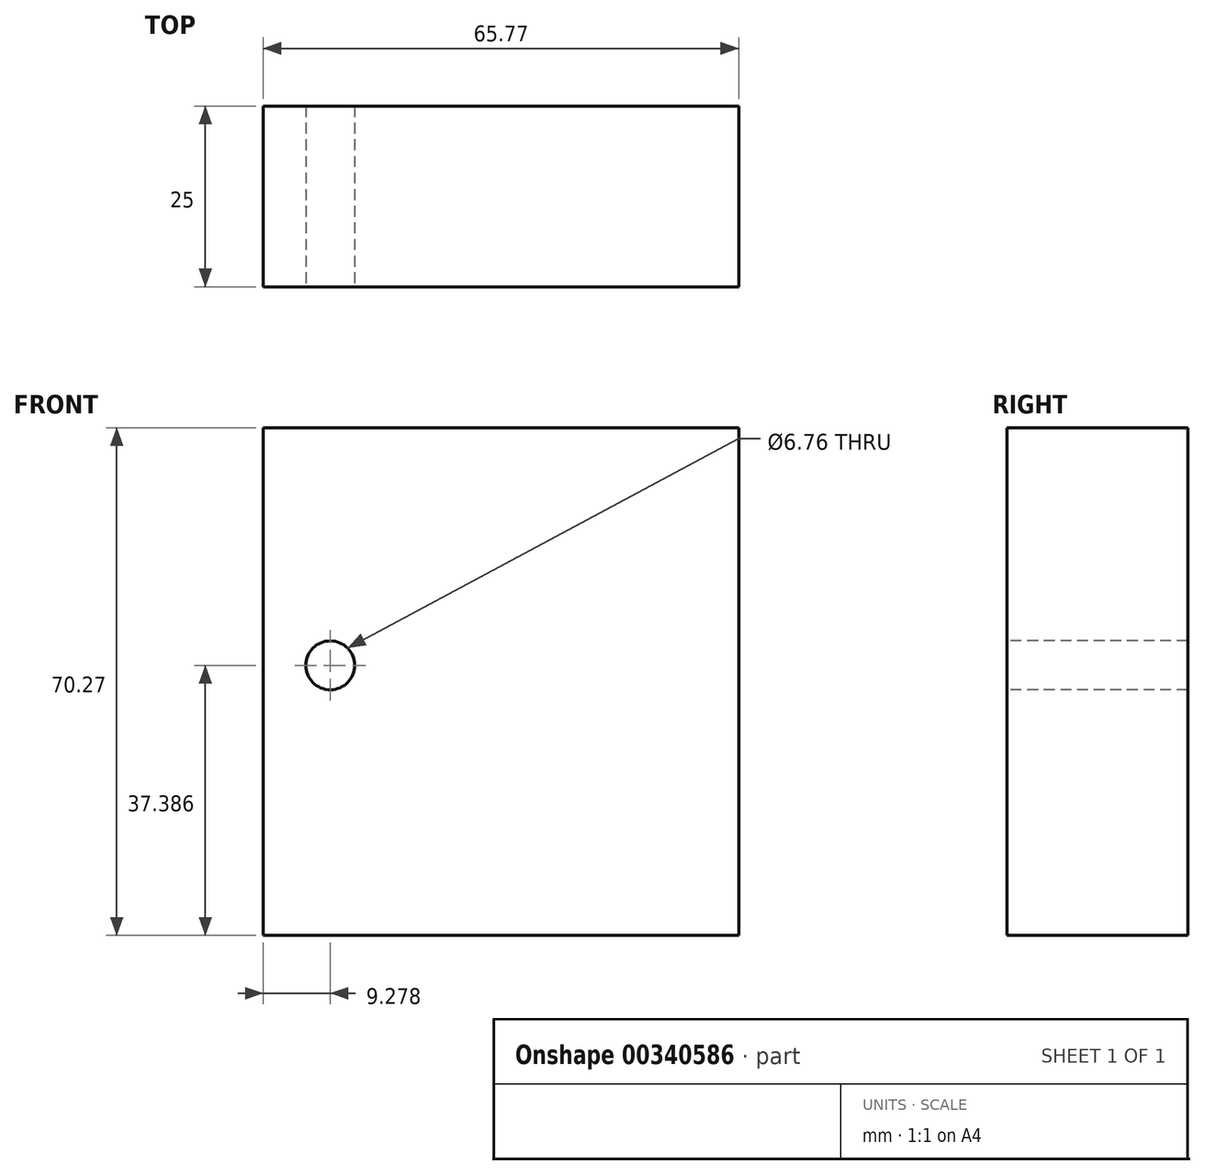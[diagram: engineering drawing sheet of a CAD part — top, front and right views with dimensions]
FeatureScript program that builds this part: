
annotation { "Feature Type Name" : "Feature", "Feature Type Description" : "" }
export const myFeature = defineFeature(function(context is Context, id is Id, definition is map)
    precondition{}
    {
        {
            var Q0;
            Q0=qCreatedBy(makeId("Front.planeOp"),FACE);
            var sketch = newSketch(context, id + "F0", { "sketchPlane" : qUnion([Q0])});
            skLineSegment(sketch, "E0.bottom", {"start": v(-98.66, -12.37) * mm, "end": v(-32.89, -12.37) * mm});
            skLineSegment(sketch, "E0.top", {"start": v(-98.66, 57.9) * mm, "end": v(-32.89, 57.9) * mm});
            skLineSegment(sketch, "E0.left", {"start": v(-98.66, -12.37) * mm, "end": v(-98.66, 57.9) * mm});
            skLineSegment(sketch, "E0.right", {"start": v(-32.89, -12.37) * mm, "end": v(-32.89, 57.9) * mm});
            skPoint(sketch, "E0.middle", {"position": v(-65.77, 22.77) * mm});
            skSolve(sketch);
        }
        {
            var Q0;
            Q0=makeQuery(id+"F0.imprint","IMPRINT",FACE,{"disambiguationData":[TD([[makeQuery(id+"F0.imprint","IMPRINT",EDGE,{"derivedFrom":sQuery(id+"F0.wireOp",EDGE,"E0.bottom")}),1.0]])]});
            extrude(context, id + "F1", {"entities" : qUnion([Q0]), "depth" : 25 * mm});
        }
        {
            var Q0;
            Q0=makeQuery(id+"F1.opExtrude","CAP_FACE",FACE,{"disambiguationData":[OSD([sQuery(id+"F0.wireOp",EDGE,"E0.bottom"),sQuery(id+"F0.wireOp",EDGE,"E0.top"),sQuery(id+"F0.wireOp",EDGE,"E0.left"),sQuery(id+"F0.wireOp",EDGE,"E0.right")])],"isStart":false});
            var sketch = newSketch(context, id + "F2", { "sketchPlane" : qUnion([Q0])});
            skPoint(sketch, "E1", {"position": v(-89.38, 25.02) * mm});
            skSolve(sketch);
        }
        {
            var Q0;
            Q0=sQuery(id+"F2.wireOp",VERTEX,"E1");
            var Q1;
            Q1=makeQuery(id+"F1.opExtrude","SWEPT_BODY",BODY,{"disambiguationData":[OSD([sQuery(id+"F0.wireOp",EDGE,"E0.bottom"),sQuery(id+"F0.wireOp",EDGE,"E0.top"),sQuery(id+"F0.wireOp",EDGE,"E0.left"),sQuery(id+"F0.wireOp",EDGE,"E0.right")])]});
            hole(context, id + "F3", {"style" : HoleStyle.SIMPLE, "endStyle" : HoleEndStyle.THROUGH, "standardTappedOrClearance" : lookupTablePath({ "standard" : "ANSI", "fit" : "Normal (ASME)", "size" : "1/4", "type" : "Clearance" }), "standardBlindInLast" : lookupTablePath({ "fit" : "Free", "standard" : "ANSI", "size" : "1/4", "type" : "Clearance" }), "holeDiameter" : 6.76 * mm, "tappedDepth" : 12 * mm, "tapClearance" : 3, "locations" : qUnion([Q0]), "scope" : qUnion([Q1])});
        }
    });
